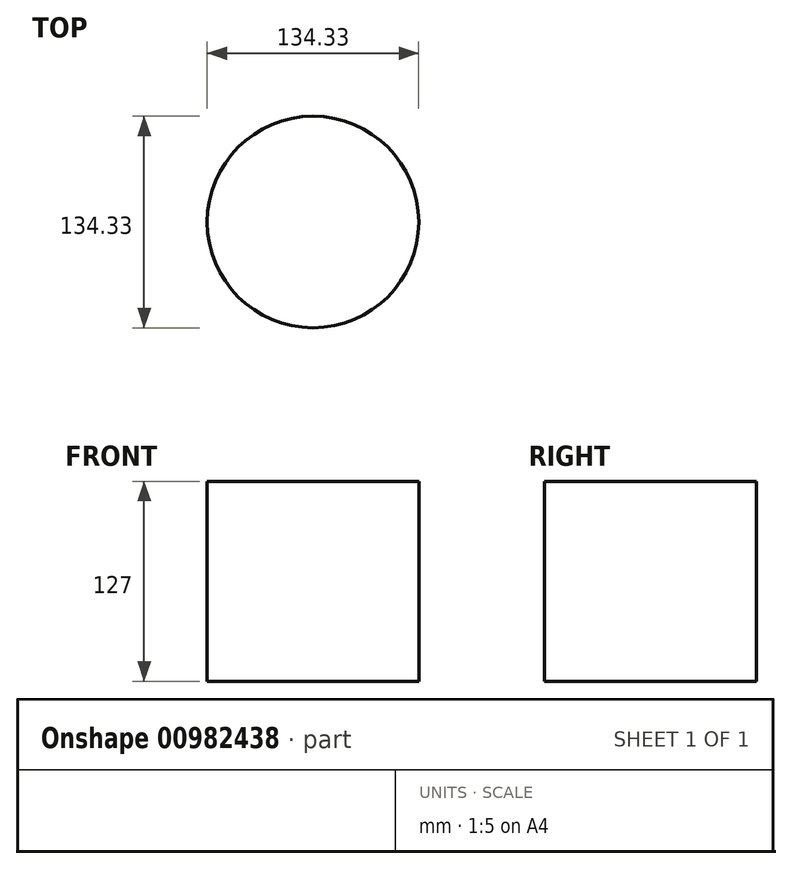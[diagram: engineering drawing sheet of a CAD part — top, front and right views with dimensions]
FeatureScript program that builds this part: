
annotation { "Feature Type Name" : "Feature", "Feature Type Description" : "" }
export const myFeature = defineFeature(function(context is Context, id is Id, definition is map)
    precondition{}
    {
        {
            var Q0;
            Q0=qCreatedBy(makeId("Top.planeOp"),FACE);
            var sketch = newSketch(context, id + "F0", { "sketchPlane" : qUnion([Q0])});
            skCircle(sketch, "E0", {"center": v(-21.67, -63.57) * mm, "radius": 67.17 * mm});
            skSolve(sketch);
        }
        {
            var Q0;
            Q0=makeQuery(id+"F0.imprint","IMPRINT",FACE,{"disambiguationData":[TD([[makeQuery(id+"F0.imprint","IMPRINT",EDGE,{"derivedFrom":sQuery(id+"F0.wireOp",EDGE,"E0")}),1.0]])]});
            var Q1;
            Q1=sQuery(id+"F0.wireOp",EDGE,"E0");
            extrude(context, id + "F1", {"entities" : qUnion([Q0]), "surfaceEntities" : qUnion([Q1]), "depth" : 127 * mm, "offsetDistance" : 25.4 * mm});
        }
    });
